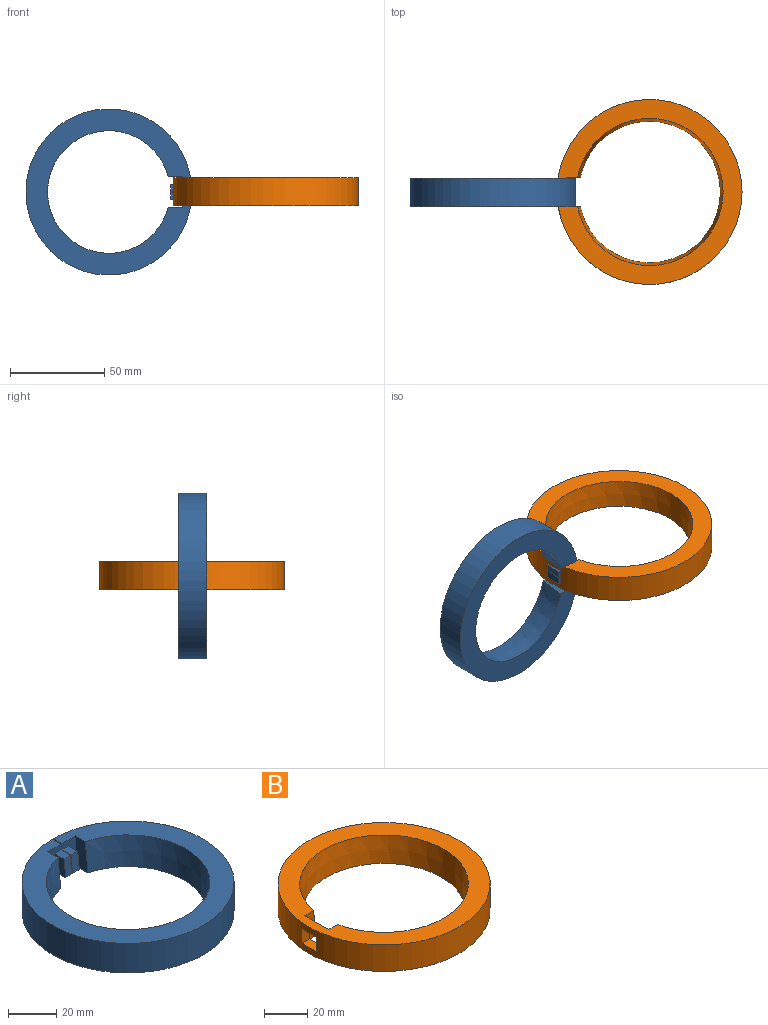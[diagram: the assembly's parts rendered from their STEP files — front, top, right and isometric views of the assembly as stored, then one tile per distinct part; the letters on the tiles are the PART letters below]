
ASSEMBLY  parts=2 mates=1
PART A: 18 faces, bbox 88x88x15 mm
  f0: plane 5.55x3.75mm, normal (0,0,1), area 20.2mm2, adj f2,f3,f8,f16
  f1: plane 6.47x3.75mm, normal (0,0,-1), area 23.7mm2, adj f2,f3,f8,f16
  f2: plane 15x7.75mm, normal (0,-1,0), area 82.5mm2, adj f0,f1,f4,f6,f8,f12,f16
  f3: cone r=34mm half-angle=5.8deg, axis (0,0,1), area 34mm2, adj f0,f1,f8,f16
  f4: plane 88x88mm, normal (0,0,1), area 2362.9mm2, adj f2,f5,f7,f12,f13,f14,f16,f17
  f5: cone r=34mm half-angle=5.8deg, axis (0,0,1), area 2904.7mm2, adj f4,f6,f12,f13
  f6: plane 88x88mm, normal (0,0,-1), area 2658.4mm2, adj f2,f5,f7,f12,f13,f14,f16,f17
  f7: cylinder r=44mm len=88mm, axis (0,0,1), area 4139.4mm2, adj f4,f6,f16,f17
  f8: plane 9x6.47mm, normal (-1,0,0), area 54.1mm2, adj f0,f1,f2,f3
  f9: plane 5.55x3.75mm, normal (0,0,1), area 20.2mm2, adj f10,f14,f15,f17
  f10: plane 9x6.47mm, normal (1,0,0), area 54.1mm2, adj f9,f11,f14,f15
  f11: plane 6.47x3.75mm, normal (0,0,-1), area 23.7mm2, adj f10,f14,f15,f17
  f12: plane 15.01x7.54mm, normal (1,0,0), area 101.2mm2, adj f2,f4,f5,f6
  f13: plane 15.01x7.54mm, normal (-1,0,0), area 101.2mm2, adj f4,f5,f6,f14
  f14: plane 15x7.75mm, normal (0,-1,0), area 82.5mm2, adj f4,f6,f9,f10,f11,f13,f17
  f15: cone r=34mm half-angle=5.8deg, axis (0,0,1), area 34mm2, adj f9,f10,f11,f17
  f16: plane 15x11.23mm, normal (1,0,0), area 126.9mm2, adj f0,f1,f2,f3,f4,f6,f7
  f17: plane 15x11.23mm, normal (-1,0,0), area 126.9mm2, adj f4,f6,f7,f9,f11,f14,f15
PART B: 11 faces, bbox 98x98x15 mm
  f0: cylinder r=49mm len=98mm, axis (0,0,1), area 4538.5mm2, adj f2,f4,f7,f8,f9,f10
  f1: plane 15.7x15mm, normal (1,0,0), area 156mm2, adj f2,f4,f5,f6,f7,f8,f9,f10
  f2: plane 98x98mm, normal (0,0,1), area 2681.9mm2, adj f0,f1,f3,f5,f6
  f3: cone r=39mm half-angle=5.8deg, axis (0,0,1), area 3383.7mm2, adj f2,f4,f5,f6
  f4: plane 98x98mm, normal (0,0,-1), area 3026.2mm2, adj f0,f1,f3,f5,f6
  f5: plane 15.01x7.37mm, normal (0,1,0), area 98.7mm2, adj f1,f2,f3,f4
  f6: plane 15.01x7.37mm, normal (0,-1,0), area 98.7mm2, adj f1,f2,f3,f4
  f7: plane 9.7x5mm, normal (0,0,-1), area 47.7mm2, adj f0,f1,f8,f10
  f8: plane 8.2x4.76mm, normal (0,1,0), area 39mm2, adj f0,f1,f7,f9
  f9: plane 9.7x5mm, normal (0,0,1), area 47.7mm2, adj f0,f1,f8,f10
  f10: plane 8.2x4.76mm, normal (0,-1,0), area 39mm2, adj f0,f1,f7,f9
PLACE A rot(axis=(-0.58,-0.58,-0.58),120deg) t=(-83,-0.35,-0.1)mm
PLACE B at identity fixed
MATE slider A.f2 <-> B.f1  axis (-1,0,0) through (-44,-4.85,-4.1)mm
